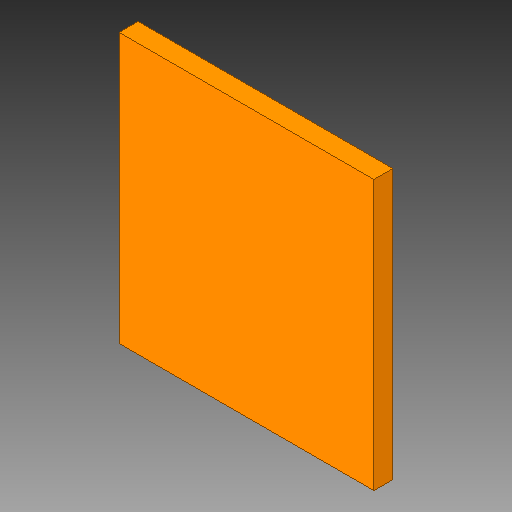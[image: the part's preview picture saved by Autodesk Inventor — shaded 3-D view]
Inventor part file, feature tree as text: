
AUTODESK INVENTOR PART (.ipt)
format: ipt  version: 2018 (Build 220112000, 112)  size: 79,360 bytes
history: native  units: in
note: dims shown in document units (in); Inventor stores cm internally (conversion verified against a paired STEP export)
features: other x1, extrude x1
ambient origin geometry x8: Origin, YZ Plane, XZ Plane, XY Plane, X Axis, Y Axis, Z Axis, Center Point
bodies: Solid1 (feature_tree)
feature tree (2):
  other  "PN80, MSP430F5529IPNR_171"
  extrude  "Extrusion1"  Depth=0.0394in TaperAngle=0.0deg
